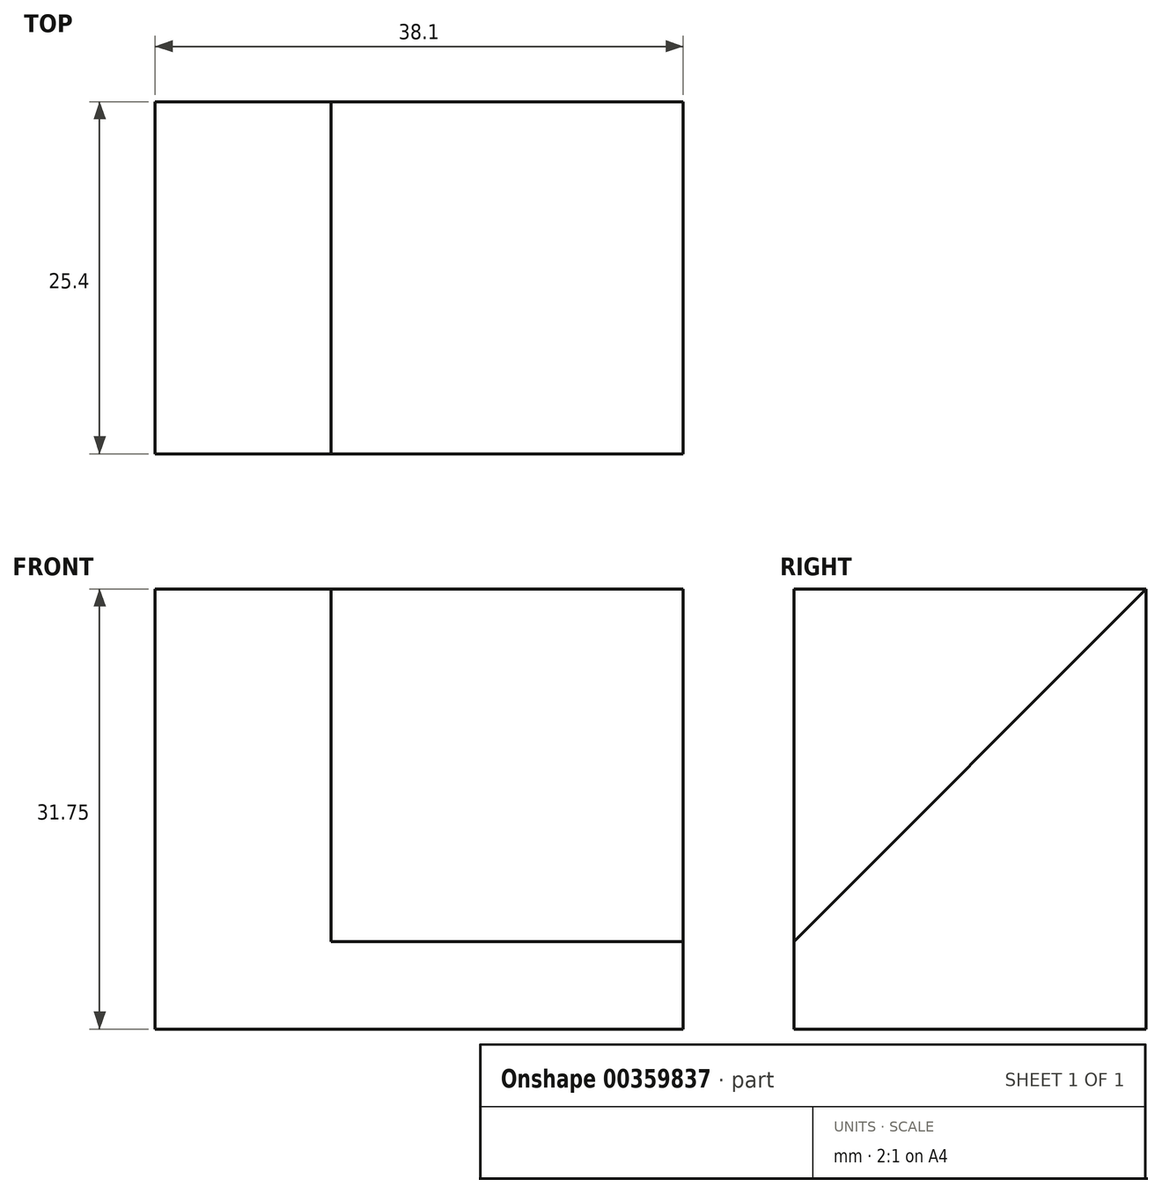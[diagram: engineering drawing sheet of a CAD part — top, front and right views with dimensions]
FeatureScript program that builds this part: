
annotation { "Feature Type Name" : "Feature", "Feature Type Description" : "" }
export const myFeature = defineFeature(function(context is Context, id is Id, definition is map)
    precondition{}
    {
        {
            var Q0;
            Q0=qCreatedBy(makeId("Front.planeOp"),FACE);
            var sketch = newSketch(context, id + "F0", { "sketchPlane" : qUnion([Q0])});
            skLineSegment(sketch, "E0", {"start": v(0, 0) * mm, "end": v(38.1, 0) * mm});
            skLineSegment(sketch, "E1", {"start": v(38.1, 0) * mm, "end": v(38.1, 31.75) * mm});
            skLineSegment(sketch, "E2", {"start": v(38.1, 31.75) * mm, "end": v(0, 31.75) * mm});
            skLineSegment(sketch, "E3", {"start": v(0, 31.75) * mm, "end": v(0, 0) * mm});
            skSolve(sketch);
        }
        {
            var Q0;
            Q0 = qSketchRegion(id + "F0", true);
            extrude(context, id + "F1", {"entities" : qUnion([Q0]), "depth" : 25.4 * mm});
        }
        {
            var Q0;
            Q0=makeQuery(id+"F1.opExtrude","SWEPT_FACE",FACE,{"disambiguationData":[OSD([sQuery(id+"F0.wireOp",EDGE,"E1")])]});
            var sketch = newSketch(context, id + "F2", { "sketchPlane" : qUnion([Q0])});
            skLineSegment(sketch, "E4", {"start": v(0, 31.75) * mm, "end": v(-25.4, 6.3) * mm});
            skLineSegment(sketch, "E5", {"start": v(-8.66, 31.75) * mm, "end": v(-8.66, 38.1) * mm});
            skLineSegment(sketch, "E6", {"start": v(-8.66, 38.1) * mm, "end": v(0, 38.1) * mm});
            skLineSegment(sketch, "E7", {"start": v(0, 38.1) * mm, "end": v(0, 31.75) * mm});
            skLineSegment(sketch, "E8", {"start": v(-25.4, 0) * mm, "end": v(-25.4, -6.35) * mm});
            skLineSegment(sketch, "E9", {"start": v(-25.4, -6.35) * mm, "end": v(-17.54, -6.35) * mm});
            skLineSegment(sketch, "E10", {"start": v(-17.54, -6.35) * mm, "end": v(-17.54, 0) * mm});
            skSolve(sketch);
        }
        {
            var Q0;
            {var subQ0=sQuery(id+"F2.wireOp",EDGE,"E4");Q0=makeQuery(id+"F2.imprint","IMPRINT",FACE,{"disambiguationData":[TD([[makeQuery(id+"F2.imprint","IMPRINT",EDGE,{"derivedFrom":subQ0}),-1.0]])]});}
            extrude(context, id + "F3", {"entities" : qUnion([Q0]), "operationType" : NewBodyOperationType.REMOVE, "oppositeDirection" : true, "depth" : 25.4 * mm});
        }
    });
